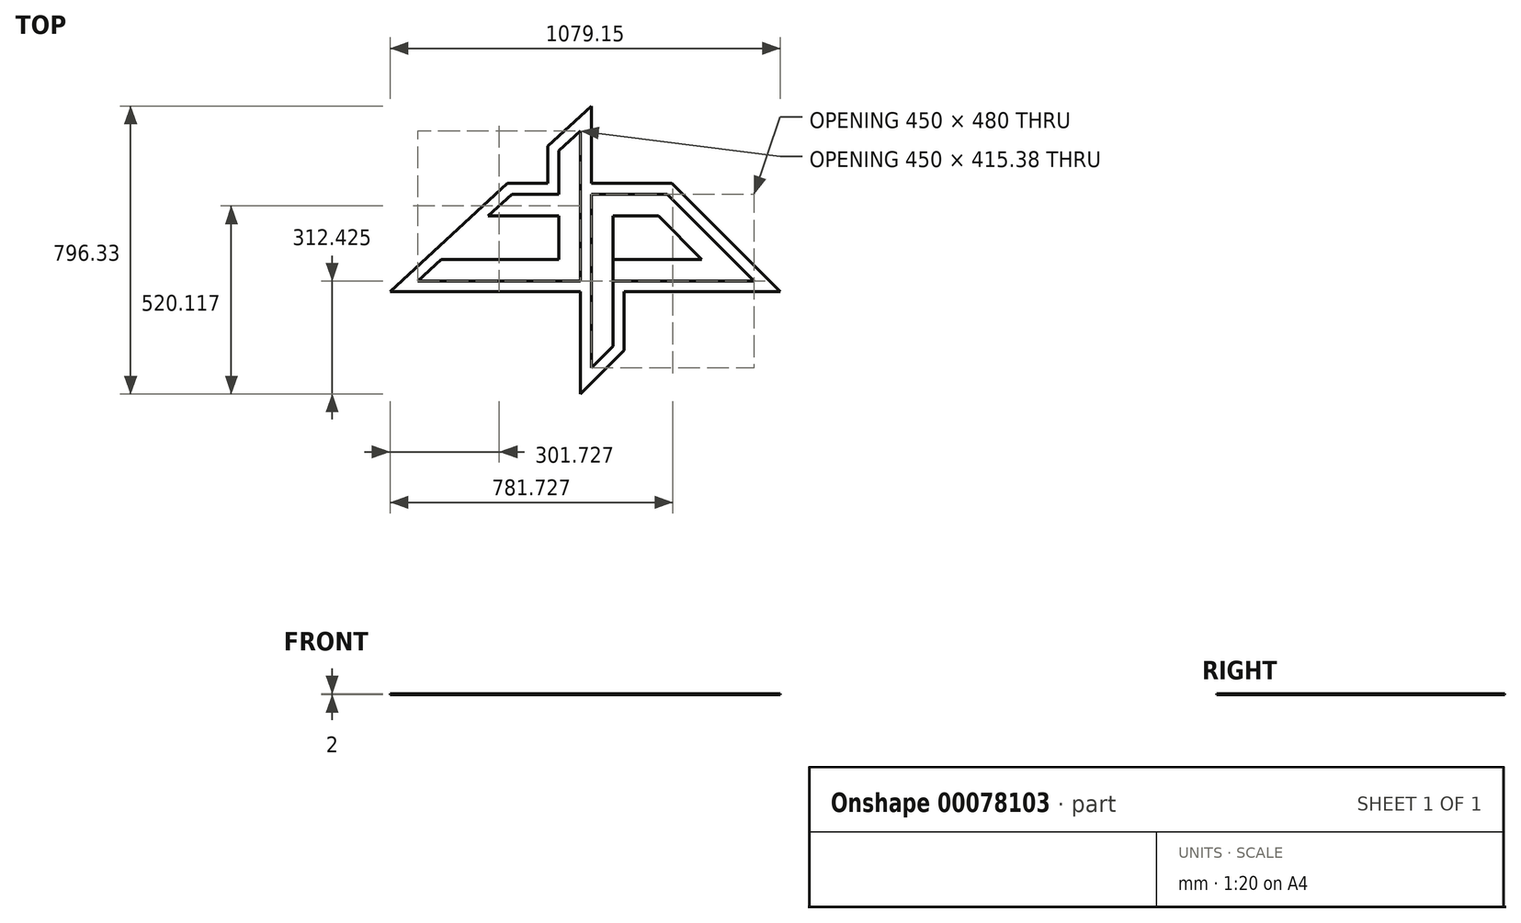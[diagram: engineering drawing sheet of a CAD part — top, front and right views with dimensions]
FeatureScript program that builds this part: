
annotation { "Feature Type Name" : "Feature", "Feature Type Description" : "" }
export const myFeature = defineFeature(function(context is Context, id is Id, definition is map)
    precondition{}
    {
        {
            var Q0;
            Q0=qCreatedBy(makeId("Top.planeOp"),FACE);
            var sketch = newSketch(context, id + "F0", { "sketchPlane" : qUnion([Q0])});
            skLineSegment(sketch, "E0", {"start": v(-409.53, 703.26) * mm, "end": v(-409.53, 189.36) * mm});
            skLineSegment(sketch, "E1", {"start": v(-409.53, -63.07) * mm, "end": v(-439.53, -93.07) * mm});
            skLineSegment(sketch, "E2", {"start": v(-439.53, -93.07) * mm, "end": v(-439.53, 675.57) * mm});
            skLineSegment(sketch, "E3", {"start": v(-439.53, 675.57) * mm, "end": v(-409.53, 703.26) * mm});
            skLineSegment(sketch, "E4", {"start": v(-439.53, 675.57) * mm, "end": v(-499.53, 620.18) * mm});
            skLineSegment(sketch, "E5", {"start": v(-439.53, 634.74) * mm, "end": v(-499.53, 579.36) * mm});
            skLineSegment(sketch, "E6", {"start": v(-499.53, 579.36) * mm, "end": v(-499.53, 459.36) * mm});
            skLineSegment(sketch, "E7", {"start": v(-499.53, 459.36) * mm, "end": v(-673.76, 459.36) * mm});
            skLineSegment(sketch, "E8", {"start": v(-673.76, 459.36) * mm, "end": v(-738.76, 399.36) * mm});
            skLineSegment(sketch, "E9", {"start": v(-738.76, 399.36) * mm, "end": v(-499.53, 399.36) * mm});
            skLineSegment(sketch, "E10", {"start": v(-499.53, 399.36) * mm, "end": v(-499.53, 279.36) * mm});
            skLineSegment(sketch, "E11", {"start": v(-499.53, 279.36) * mm, "end": v(-868.76, 279.36) * mm});
            skLineSegment(sketch, "E12", {"start": v(-868.76, 279.36) * mm, "end": v(-933.76, 219.36) * mm});
            skLineSegment(sketch, "E13", {"start": v(-933.76, 219.36) * mm, "end": v(-439.53, 219.36) * mm});
            skLineSegment(sketch, "E14", {"start": v(-499.53, 620.18) * mm, "end": v(-966.26, 189.36) * mm});
            skLineSegment(sketch, "E15", {"start": v(-499.53, 579.36) * mm, "end": v(-922.03, 189.36) * mm});
            skLineSegment(sketch, "E16", {"start": v(-966.26, 189.36) * mm, "end": v(-439.53, 189.36) * mm});
            skLineSegment(sketch, "E17", {"start": v(-409.53, 459.36) * mm, "end": v(-157.1, 459.36) * mm});
            skLineSegment(sketch, "E18", {"start": v(-157.1, 459.36) * mm, "end": v(112.9, 189.36) * mm});
            skLineSegment(sketch, "E19", {"start": v(112.9, 189.36) * mm, "end": v(-409.53, 189.36) * mm});
            skLineSegment(sketch, "E20", {"start": v(-409.53, 399.36) * mm, "end": v(-139.53, 399.36) * mm});
            skLineSegment(sketch, "E21", {"start": v(-139.53, 399.36) * mm, "end": v(40.47, 219.36) * mm});
            skLineSegment(sketch, "E22", {"start": v(40.47, 219.36) * mm, "end": v(-349.53, 219.36) * mm});
            skLineSegment(sketch, "E23", {"start": v(-349.53, 219.36) * mm, "end": v(-349.53, 399.36) * mm});
            skLineSegment(sketch, "E24", {"start": v(-499.53, 620.18) * mm, "end": v(-499.53, 579.36) * mm});
            skLineSegment(sketch, "E25", {"start": v(-641.26, 489.36) * mm, "end": v(-529.53, 489.36) * mm});
            skLineSegment(sketch, "E26", {"start": v(-529.53, 489.36) * mm, "end": v(-529.53, 592.49) * mm});
            skLineSegment(sketch, "E27", {"start": v(-409.53, 489.36) * mm, "end": v(-187.1, 489.36) * mm});
            skLineSegment(sketch, "E28", {"start": v(-224.39, 399.36) * mm, "end": v(-44.39, 219.36) * mm});
            skLineSegment(sketch, "E29", {"start": v(-139.53, 399.36) * mm, "end": v(-199.53, 459.36) * mm});
            skLineSegment(sketch, "E30", {"start": v(-104.39, 279.36) * mm, "end": v(-409.53, 279.36) * mm});
            skLineSegment(sketch, "E31", {"start": v(-349.53, 219.36) * mm, "end": v(-349.53, -3.07) * mm});
            skLineSegment(sketch, "E32", {"start": v(-349.53, -3.07) * mm, "end": v(-409.53, -63.07) * mm});
            skLineSegment(sketch, "E33", {"start": v(-349.53, -3.07) * mm, "end": v(-319.53, 26.93) * mm});
            skLineSegment(sketch, "E34", {"start": v(-319.53, 26.93) * mm, "end": v(-319.53, 189.36) * mm});
            skLineSegment(sketch, "E35", {"start": v(-409.53, -20.64) * mm, "end": v(-349.53, 39.36) * mm});
            skLineSegment(sketch, "E36", {"start": v(-349.53, 279.36) * mm, "end": v(-349.53, 219.36) * mm});
            skPoint(sketch, "E37", {"position": v(-889.53, 219.36) * mm});
            skLineSegment(sketch, "E38", {"start": v(-409.53, 189.36) * mm, "end": v(-409.53, -63.07) * mm});
            skLineSegment(sketch, "E39", {"start": v(-157.1, 459.36) * mm, "end": v(-187.1, 489.36) * mm});
            skSolve(sketch);
        }
        {
            var Q0;
            {var subQ0=sQuery(id+"F0.wireOp",EDGE,"E23");var subQ1=sQuery(id+"F0.wireOp",EDGE,"E20");var subQ2=makeQuery(id+"F0.imprint","INTERSECT",VERTEX,{"derivedFrom":[subQ1,subQ0]});Q0=makeQuery(id+"F0.imprint","IMPRINT",FACE,{"disambiguationData":[TD([[makeQuery(id+"F0.imprint","IMPRINT",EDGE,{"disambiguationData":[TD([[subQ2,-1.0]])],"derivedFrom":subQ1}),-1.0]])]});}
            var Q1;
            {var subQ0=sQuery(id+"F0.wireOp",EDGE,"E14");var subQ1=sQuery(id+"F0.wireOp",EDGE,"E13");var subQ2=makeQuery(id+"F0.imprint","INTERSECT",VERTEX,{"derivedFrom":[subQ1,subQ0]});Q1=makeQuery(id+"F0.imprint","IMPRINT",FACE,{"disambiguationData":[TD([[makeQuery(id+"F0.imprint","IMPRINT",EDGE,{"disambiguationData":[TD([[subQ2,-1.0]])],"derivedFrom":subQ1}),-1.0]])]});}
            var Q2;
            {var subQ0=sQuery(id+"F0.wireOp",EDGE,"E13");var subQ1=sQuery(id+"F0.wireOp",EDGE,"E2");var subQ2=makeQuery(id+"F0.imprint","INTERSECT",VERTEX,{"derivedFrom":[subQ1,subQ0]});Q2=makeQuery(id+"F0.imprint","IMPRINT",FACE,{"disambiguationData":[TD([[makeQuery(id+"F0.imprint","IMPRINT",EDGE,{"disambiguationData":[TD([[subQ2,1.0]])],"derivedFrom":subQ1}),1.0]])]});}
            var Q3;
            {var subQ0=sQuery(id+"F0.wireOp",EDGE,"E14");var subQ1=sQuery(id+"F0.wireOp",EDGE,"E7");var subQ2=makeQuery(id+"F0.imprint","INTERSECT",VERTEX,{"derivedFrom":[subQ1,subQ0]});Q3=makeQuery(id+"F0.imprint","IMPRINT",FACE,{"disambiguationData":[TD([[makeQuery(id+"F0.imprint","IMPRINT",EDGE,{"disambiguationData":[TD([[subQ2,1.0]])],"derivedFrom":subQ1}),1.0]])]});}
            var Q4;
            {var subQ0=sQuery(id+"F0.wireOp",EDGE,"E14");var subQ1=sQuery(id+"F0.wireOp",EDGE,"E9");var subQ2=makeQuery(id+"F0.imprint","INTERSECT",VERTEX,{"derivedFrom":[subQ1,subQ0]});Q4=makeQuery(id+"F0.imprint","IMPRINT",FACE,{"disambiguationData":[TD([[makeQuery(id+"F0.imprint","IMPRINT",EDGE,{"disambiguationData":[TD([[subQ2,-1.0]])],"derivedFrom":subQ1}),-1.0]])]});}
            var Q5;
            {var subQ0=sQuery(id+"F0.wireOp",EDGE,"E14");var subQ1=sQuery(id+"F0.wireOp",EDGE,"E11");var subQ2=makeQuery(id+"F0.imprint","INTERSECT",VERTEX,{"derivedFrom":[subQ1,subQ0]});Q5=makeQuery(id+"F0.imprint","IMPRINT",FACE,{"disambiguationData":[TD([[makeQuery(id+"F0.imprint","IMPRINT",EDGE,{"disambiguationData":[TD([[subQ2,1.0]])],"derivedFrom":subQ1}),1.0]])]});}
            var Q6;
            {var subQ1=sQuery(id+"F0.wireOp",EDGE,"E1");Q6=makeQuery(id+"F0.imprint","IMPRINT",FACE,{"disambiguationData":[TD([[makeQuery(id+"F0.imprint","IMPRINT",EDGE,{"derivedFrom":subQ1}),-1.0]])]});}
            var Q7;
            {var subQ0=sQuery(id+"F0.wireOp",EDGE,"E4");Q7=makeQuery(id+"F0.imprint","IMPRINT",FACE,{"disambiguationData":[TD([[makeQuery(id+"F0.imprint","IMPRINT",EDGE,{"derivedFrom":subQ0}),1.0]])]});}
            var Q8;
            {var subQ0=sQuery(id+"F0.wireOp",EDGE,"E10");Q8=makeQuery(id+"F0.imprint","IMPRINT",FACE,{"disambiguationData":[TD([[makeQuery(id+"F0.imprint","IMPRINT",EDGE,{"derivedFrom":subQ0}),-1.0]])]});}
            var Q9;
            {var subQ0=sQuery(id+"F0.wireOp",EDGE,"E14");var subQ1=sQuery(id+"F0.wireOp",EDGE,"E7");var subQ2=makeQuery(id+"F0.imprint","INTERSECT",VERTEX,{"derivedFrom":[subQ1,subQ0]});Q9=makeQuery(id+"F0.imprint","IMPRINT",FACE,{"disambiguationData":[TD([[makeQuery(id+"F0.imprint","IMPRINT",EDGE,{"disambiguationData":[TD([[subQ2,1.0]])],"derivedFrom":subQ1}),-1.0]])]});}
            var Q10;
            {var subQ5=sQuery(id+"F0.wireOp",EDGE,"E6");Q10=makeQuery(id+"F0.imprint","IMPRINT",FACE,{"disambiguationData":[TD([[makeQuery(id+"F0.imprint","IMPRINT",EDGE,{"derivedFrom":subQ5}),-1.0]])]});}
            var Q11;
            {var subQ0=sQuery(id+"F0.wireOp",EDGE,"E24");Q11=makeQuery(id+"F0.imprint","IMPRINT",FACE,{"disambiguationData":[TD([[makeQuery(id+"F0.imprint","IMPRINT",EDGE,{"derivedFrom":subQ0}),-1.0]])]});}
            var Q12;
            {var subQ3=sQuery(id+"F0.wireOp",EDGE,"E27");Q12=makeQuery(id+"F0.imprint","IMPRINT",FACE,{"disambiguationData":[TD([[makeQuery(id+"F0.imprint","IMPRINT",EDGE,{"derivedFrom":subQ3}),-1.0]])]});}
            var Q13;
            {var subQ1=sQuery(id+"F0.wireOp",EDGE,"E18");Q13=makeQuery(id+"F0.imprint","IMPRINT",FACE,{"disambiguationData":[TD([[makeQuery(id+"F0.imprint","IMPRINT",EDGE,{"derivedFrom":subQ1}),-1.0]])]});}
            var Q14;
            {var subQ4=sQuery(id+"F0.wireOp",EDGE,"E33");Q14=makeQuery(id+"F0.imprint","IMPRINT",FACE,{"disambiguationData":[TD([[makeQuery(id+"F0.imprint","IMPRINT",EDGE,{"derivedFrom":subQ4}),1.0]])]});}
            var Q15;
            {var subQ0=sQuery(id+"F0.wireOp",EDGE,"E32");Q15=makeQuery(id+"F0.imprint","IMPRINT",FACE,{"disambiguationData":[TD([[makeQuery(id+"F0.imprint","IMPRINT",EDGE,{"derivedFrom":subQ0}),-1.0]])]});}
            var Q16;
            {var subQ3=sQuery(id+"F0.wireOp",EDGE,"E36");Q16=makeQuery(id+"F0.imprint","IMPRINT",FACE,{"disambiguationData":[TD([[makeQuery(id+"F0.imprint","IMPRINT",EDGE,{"derivedFrom":subQ3}),-1.0]])]});}
            extrude(context, id + "F1", {"entities" : qUnion([Q0, Q1, Q2, Q3, Q4, Q5, Q6, Q7, Q8, Q9, Q10, Q11, Q12, Q13, Q14, Q15, Q16]), "depth" : 2 * mm});
        }
    });
